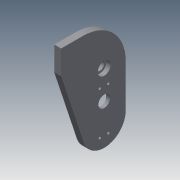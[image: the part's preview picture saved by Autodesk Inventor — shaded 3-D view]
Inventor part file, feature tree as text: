
AUTODESK INVENTOR PART (.ipt)
format: ipt  version: 2013 (Build 170138000, 138)  size: 183,296 bytes
history: native  units: mm
features: extrude x7, sketch x7, fillet x1
ambient origin geometry x8: Origin, YZ Plane, XZ Plane, XY Plane, X Axis, Y Axis, Z Axis, Center Point
bodies: Solid1 (feature_tree)
feature tree (15):
  extrude  "Extrusion1"  Depth=66.3mm
  extrude  "Extrusion2"  Depth=55.0mm
  extrude  "Extrusion3"  Depth=55.0mm
  extrude  "Extrusion4"  Depth=9.9mm
  extrude  "Extrusion5"  Depth=9.9mm
  extrude  "Extrusion6"  Depth=3.0mm
  extrude  "Extrusion7"  Depth=3.0mm
  fillet  "Fillet1"  Radius=3.0mm
  sketch  "Sketch1"  dims[d0=33.15mm d2=66.3mm]
  sketch  "Sketch2"  dims[d4=18.1mm d5=55.0mm]
  sketch  "Sketch3"  dims[d6=20.0mm d7=55.0mm]
  sketch  "Sketch4"  dims[d8=40.2mm d9=9.9mm]
  sketch  "Sketch5"  dims[d10=9.5mm d11=9.9mm]
  sketch  "Sketch6"  dims[d12=9.5mm d13=3.0mm]
  sketch  "Sketch7"  dims[d14=3.0mm d15=3.0mm d16=3.0mm d17=13.6mm d20=25.0mm d21=45.0mm d22=15.0mm d23=5.0mm d24=0.0mm d25=5.0mm d26=0.0mm d27=25.0mm d28=28.0mm d29=5.0mm d30=0.0mm d31=3.0mm d32=0.0mm d33=40.5mm d34=20.0mm d35=3.0mm d36=0.0mm d37=1.0mm d38=0.0mm d39=10.0mm d40=3.0mm d41=0.0mm d42=1.0mm]
